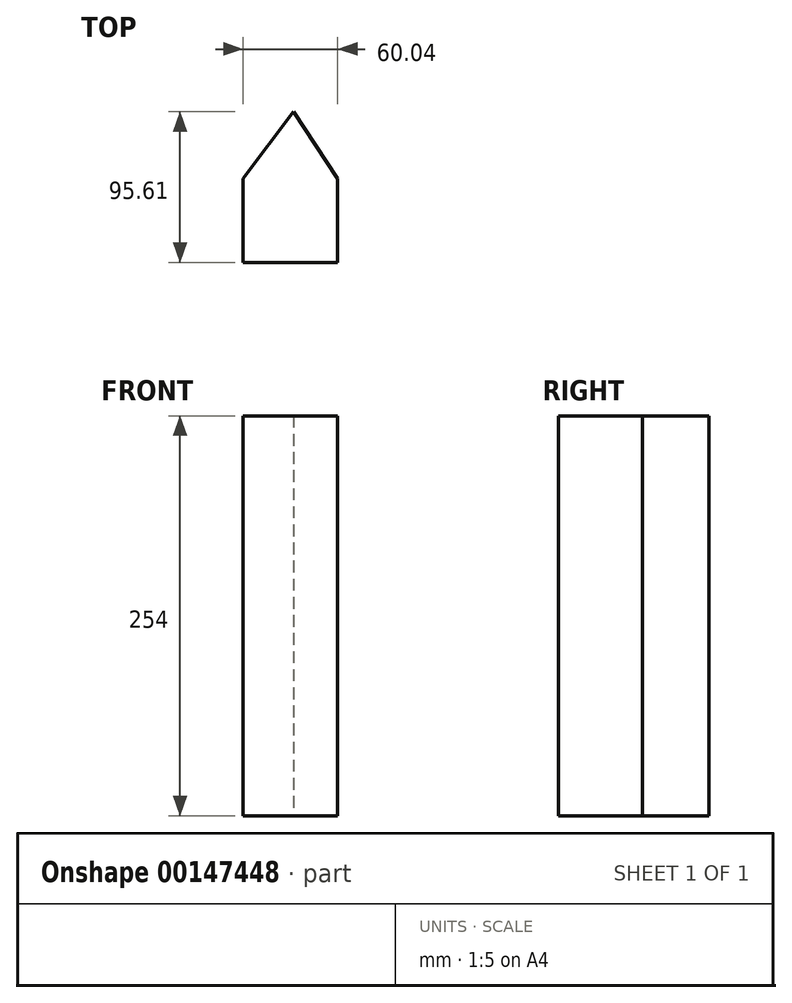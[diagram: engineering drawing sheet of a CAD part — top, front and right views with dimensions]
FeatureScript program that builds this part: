
annotation { "Feature Type Name" : "Feature", "Feature Type Description" : "" }
export const myFeature = defineFeature(function(context is Context, id is Id, definition is map)
    precondition{}
    {
        {
            var Q0;
            Q0=qCreatedBy(makeId("Top.planeOp"),FACE);
            var sketch = newSketch(context, id + "F0", { "sketchPlane" : qUnion([Q0])});
            skLineSegment(sketch, "E0", {"start": v(0, 55.82) * mm, "end": v(-32.06, 13.55) * mm});
            skLineSegment(sketch, "E1", {"start": v(-32.06, 13.55) * mm, "end": v(-32.06, -39.79) * mm});
            skLineSegment(sketch, "E2", {"start": v(-32.06, -39.79) * mm, "end": v(27.98, -39.79) * mm});
            skLineSegment(sketch, "E3", {"start": v(27.98, -39.79) * mm, "end": v(27.98, 13.55) * mm});
            skLineSegment(sketch, "E4", {"start": v(27.98, 13.55) * mm, "end": v(0, 55.82) * mm});
            skSolve(sketch);
        }
        {
            var Q0;
            Q0=makeQuery(id+"F0.imprint","IMPRINT",FACE,{"disambiguationData":[TD([[makeQuery(id+"F0.imprint","IMPRINT",EDGE,{"derivedFrom":sQuery(id+"F0.wireOp",EDGE,"E0")}),1.0]])]});
            extrude(context, id + "F1", {"entities" : qUnion([Q0]), "depth" : 254 * mm});
        }
    });
